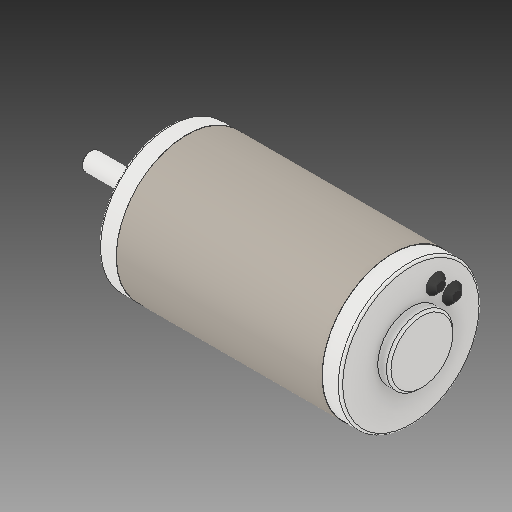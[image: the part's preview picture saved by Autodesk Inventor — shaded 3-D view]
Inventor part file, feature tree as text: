
AUTODESK INVENTOR PART (.ipt)
format: ipt  version: 2018 (Build 220112000, 112)  size: 163,328 bytes
history: native  units: in
note: dims shown in document units (in); Inventor stores cm internally (conversion verified against a paired STEP export)
features: chamfer x1
ambient origin geometry x8: Origin, YZ Plane, XZ Plane, XY Plane, X Axis, Y Axis, Z Axis, Center Point
bodies: Solid1 (feature_tree)
feature tree (1):
  chamfer  "Chamfer3"  [1 undecoded]
note: 1 required parameter value undecoded (feature->parameter linkage not recoverable at this tier; creation-order binding heuristic only, values carry confidence <= 0.55)
